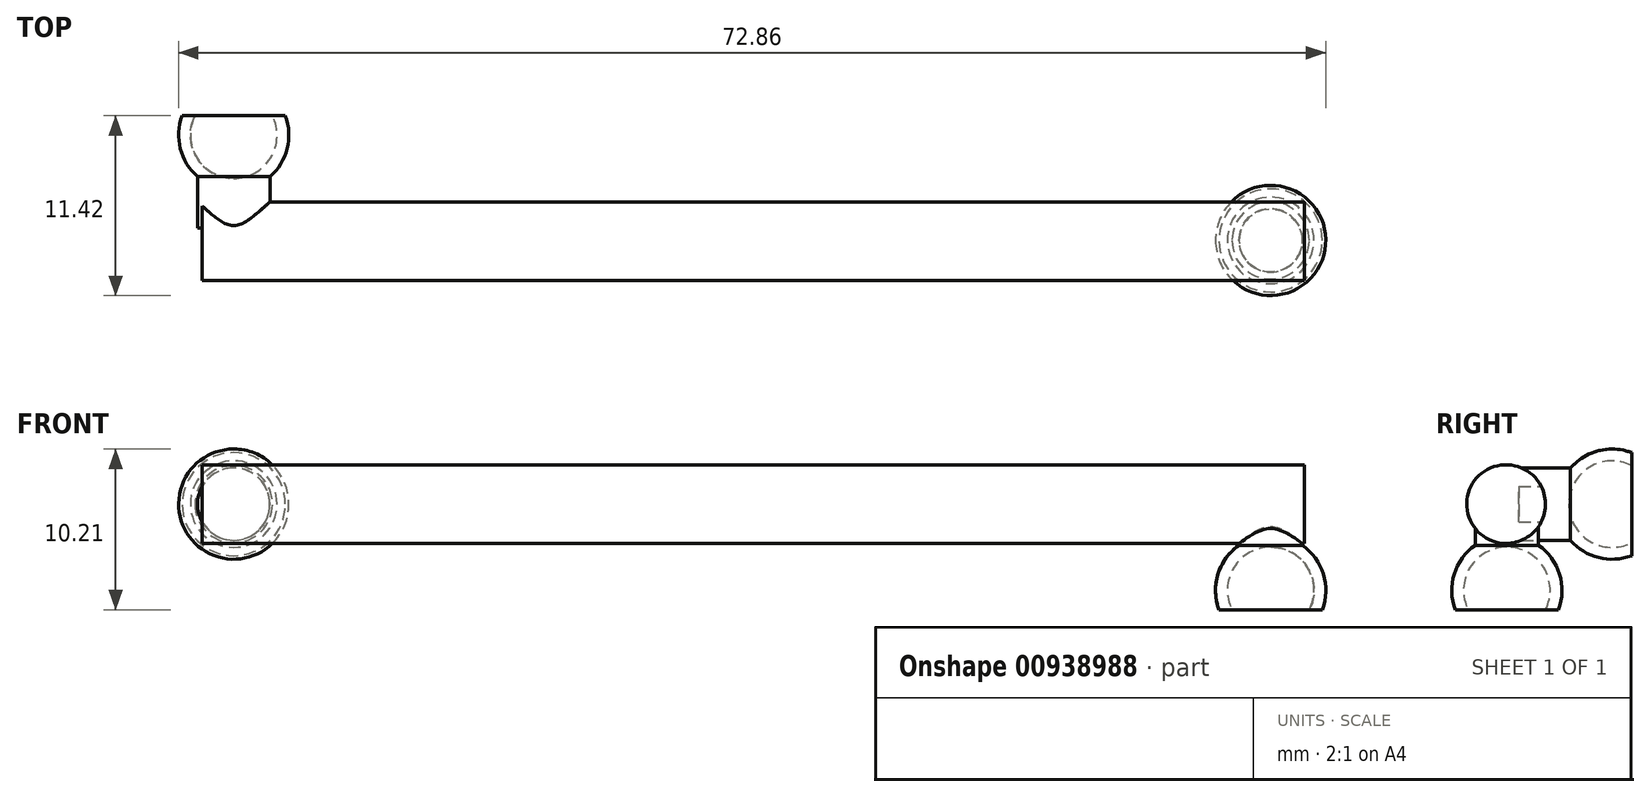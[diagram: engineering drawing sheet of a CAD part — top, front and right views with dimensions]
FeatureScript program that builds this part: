
annotation { "Feature Type Name" : "Feature", "Feature Type Description" : "" }
export const myFeature = defineFeature(function(context is Context, id is Id, definition is map)
    precondition{}
    {
        {
            var Q0;
            Q0=qCreatedBy(makeId("Top.planeOp"),FACE);
            var sketch = newSketch(context, id + "F0", { "sketchPlane" : qUnion([Q0])});
            skLineSegment(sketch, "E0", {"start": v(0.76, 6.94) * mm, "end": v(7.53, 6.94) * mm, "construction": true});
            skLineSegment(sketch, "E1.MirrorCS", {"start": v(3, 7.97) * mm, "end": v(5.3, 7.97) * mm});
            skArc(sketch, "E2.MirrorCS", {"start": v(6.27, 15.12) * mm, "mid": v(5.88, 11.9) * mm, "end": v(3, 10.39) * mm});
            skLineSegment(sketch, "E3.MirrorCS", {"start": v(3, 13.89) * mm, "end": v(3, 10.39) * mm});
            skLineSegment(sketch, "E4.MirrorCS", {"start": v(5.46, 15.12) * mm, "end": v(6.27, 15.12) * mm});
            skLineSegment(sketch, "E5.MirrorCS", {"start": v(5.3, 7.97) * mm, "end": v(5.3, 10.77) * mm});
            skLineSegment(sketch, "E6.MirrorCS", {"start": v(3, 13.89) * mm, "end": v(3, 16.9) * mm});
            skLineSegment(sketch, "E7.MirrorCS", {"start": v(3, 10.39) * mm, "end": v(3, 7.97) * mm});
            skArc(sketch, "E8.MirrorCS", {"start": v(5.46, 15.12) * mm, "mid": v(5.34, 12.44) * mm, "end": v(3, 11.14) * mm});
            skLineSegment(sketch, "E9", {"start": v(5.3, 10.77) * mm, "end": v(5.3, 11.25) * mm});
            skSolve(sketch);
        }
        {
            var Q0;
            Q0=makeQuery(id+"F0.imprint","IMPRINT",FACE,{"disambiguationData":[TD([[makeQuery(id+"F0.imprint","IMPRINT",EDGE,{"derivedFrom":sQuery(id+"F0.wireOp",EDGE,"E1.MirrorCS")}),1.0]])]});
            var Q1;
            {var subQ0=sQuery(id+"F0.wireOp",EDGE,"E4.MirrorCS");Q1=makeQuery(id+"F0.imprint","IMPRINT",FACE,{"disambiguationData":[TD([[makeQuery(id+"F0.imprint","IMPRINT",EDGE,{"derivedFrom":subQ0}),-1.0]])]});}
            var Q2;
            Q2=sQuery(id+"F0.wireOp",EDGE,"E3.MirrorCS");
            revolve(context, id + "F1", {"surfaceOperationType" : NewSurfaceOperationType.NEW, "entities" : qUnion([Q0, Q1]), "axis" : qUnion([Q2]), "revolveType" : RevolveType.FULL});
        }
        {
            var Q0;
            Q0=qCreatedBy(makeId("Right.planeOp"),FACE);
            cPlane(context, id + "F2", {"entities" : qUnion([Q0]), "cplaneType" : CPlaneType.OFFSET, "offset" : 36 * mm, "width" : 150 * mm, "height" : 150 * mm});
        }
        {
            var Q0;
            Q0=qCreatedBy(id+"F2.planeOp",FACE);
            var sketch = newSketch(context, id + "F3", { "sketchPlane" : qUnion([Q0])});
            skCircle(sketch, "E10", {"center": v(7.15, 0) * mm, "radius": 2.5 * mm});
            skSolve(sketch);
        }
        {
            var Q0;
            Q0=makeQuery(id+"F3.imprint","IMPRINT",FACE,{"disambiguationData":[TD([[makeQuery(id+"F3.imprint","IMPRINT",EDGE,{"derivedFrom":sQuery(id+"F3.wireOp",EDGE,"E10")}),1.0]])]});
            extrude(context, id + "F4", {"entities" : qUnion([Q0]), "operationType" : NewBodyOperationType.ADD, "depth" : 70 * mm, "offsetDistance" : 25 * mm, "symmetric" : true});
        }
        {
            var Q0;
            Q0=makeQuery(id+"F1.opRevolve","SWEPT_BODY",BODY,{"disambiguationData":[OSD([sQuery(id+"F0.wireOp",EDGE,"E1.MirrorCS"),sQuery(id+"F0.wireOp",EDGE,"E2.MirrorCS"),sQuery(id+"F0.wireOp",EDGE,"E3.MirrorCS"),sQuery(id+"F0.wireOp",EDGE,"E4.MirrorCS"),sQuery(id+"F0.wireOp",EDGE,"E5.MirrorCS"),sQuery(id+"F0.wireOp",EDGE,"E7.MirrorCS"),sQuery(id+"F0.wireOp",EDGE,"E8.MirrorCS")])]});
            transform(context, id + "F5", {"entities" : qUnion([Q0]), "transformType" : TransformType.TRANSLATION_3D, "dx" : 0 * mm, "dy" : -7.2 * mm, "dz" : 0 * mm, "makeCopy" : false});
        }
        {
            var Q0;
            Q0=qCreatedBy(makeId("Front.planeOp"),FACE);
            var sketch = newSketch(context, id + "F6", { "sketchPlane" : qUnion([Q0])});
            skLineSegment(sketch, "E11", {"start": v(68.86, -5.48) * mm, "end": v(68.86, -8.5) * mm});
            skArc(sketch, "E12", {"start": v(71.32, -6.71) * mm, "mid": v(71.2, -4.03) * mm, "end": v(68.86, -2.73) * mm});
            skArc(sketch, "E13", {"start": v(72.13, -6.71) * mm, "mid": v(71.74, -3.49) * mm, "end": v(68.86, -1.98) * mm});
            skLineSegment(sketch, "E14.trimOffspring", {"start": v(71.32, -6.71) * mm, "end": v(72.13, -6.71) * mm});
            skLineSegment(sketch, "E15", {"start": v(68.86, -5.48) * mm, "end": v(68.86, -1.98) * mm});
            skLineSegment(sketch, "E16", {"start": v(68.86, -1.98) * mm, "end": v(68.86, 0.43) * mm});
            skLineSegment(sketch, "E17", {"start": v(68.86, 0.43) * mm, "end": v(70.87, 0.43) * mm});
            skLineSegment(sketch, "E18", {"start": v(70.87, 0.43) * mm, "end": v(70.87, -2.61) * mm});
            skSolve(sketch);
        }
        {
            var Q0;
            {var subQ5=sQuery(id+"F6.wireOp",EDGE,"E12");Q0=makeQuery(id+"F6.imprint","IMPRINT",FACE,{"disambiguationData":[TD([[makeQuery(id+"F6.imprint","IMPRINT",EDGE,{"derivedFrom":subQ5}),-1.0]])]});}
            var Q1;
            {var subQ0=sQuery(id+"F6.wireOp",EDGE,"E16");Q1=makeQuery(id+"F6.imprint","IMPRINT",FACE,{"disambiguationData":[TD([[makeQuery(id+"F6.imprint","IMPRINT",EDGE,{"derivedFrom":subQ0}),-1.0]])]});}
            var Q2;
            Q2=sQuery(id+"F6.wireOp",EDGE,"E15");
            revolve(context, id + "F7", {"operationType" : NewBodyOperationType.ADD, "surfaceOperationType" : NewSurfaceOperationType.NEW, "entities" : qUnion([Q0, Q1]), "axis" : qUnion([Q2]), "revolveType" : RevolveType.FULL});
        }
    });
